# Revit family: QF_ELECTROLUXPROFESSIONAL_588552_MBBABBDOAO
name_source: partatom
category: Specialty Equipment
revit_build: Autodesk Revit 2018 (Build: 20190510_1515(x64)
units: mm (PartAtom-declared; Revit-internal decimal feet)

## family parameters
Always vertical = Yes
Cut with Voids When Loaded = No
Part Type = Normal
Room Calculation Point = No
Round Connector Dimension = Use Diameter
Shared = No
Work Plane-Based = No

## types (1)
- QF_ELECTROLUX_588552_MBBABBDOAO
    Accessory = Yes
    Cold Water Connection Height = 0 mm  [stored 0 ft]
    Cold Water Maximum Pressure = 0.00 psi
    Cold Water Minimum Pressure = 0.00 psi
    Cold Water Size = 1"
    Compressed Air Pressure = 0.00 psi
    Compressed Air Size = 0"
    Compressed Air Volume = 0 GPM
    Condensate Return Size = 0"
    Conn Conduit = Yes
    Depth Actual = 850 mm  [stored 2.78871 ft]
    Description = EL.BAINM,1/1GN,TAP(B),1S,BS,400X850X250H
    Direct Waste Size = 1"
    Electrical Remarks = 400 V/3N ph/50/60 Hz
    Gas Input Pressure = 0.0
    Gas KW = 0
    Gas Size = 0"
    HP = 2 HP
    Height Actual = 250 mm  [stored 0.82021 ft]
    Hot Water Connection Height = 0 mm  [stored 0 ft]
    Hot Water Consumption = 0 GPM
    Hot Water Maximum Pressure = 0.00 psi
    Hot Water Minimum Pressure = 0.00 psi
    Hot Water Size = 1"
    Hot Water Temperature = -460 °F
    Indirect Waste Connection Height = 0 mm  [stored 0 ft]
    Indirect Waste Size = 1"
    Length Actual = 400 mm  [stored 1.31234 ft]
    Manufacturer = Electrolux
    Max Overcurrent Protection = 0 A
    Min Ckt Ampacity = 0 A
    Model = MBBABBDOAO
    Phase = 3
    Refrigerant Compressor Remote = Yes
    Refrigeration Liquid Line Size = 0"
    Refrigeration Suction Line Size = 0"
    Steam Pounds per Hour = 0
    Steam Supply Maximum Pressure = 0.00 psi
    Steam Supply Minimum Pressure = 0.00 psi
    Steam Supply Size = 0"
    URL = http://professional.electrolux.com
    URL Manufacturer = http://professional.electrolux.com
    Volts = 400 V
    Watts = 1500 W
    Weight = 9.07 kg
    Weight in Pounds = 55.1

note: source unit labels omitted for Gas Input Pressure — the stored unit's dimension contradicts the parameter name (converter mislabeling)

note: [stored X ft] marks values corroborated as IEEE doubles in the binary element streams (Revit-internal decimal feet)

## geometry (parser evidence)
native form markers: Blend x40, Sweep x7
no freeform markers — native parametric forms only
